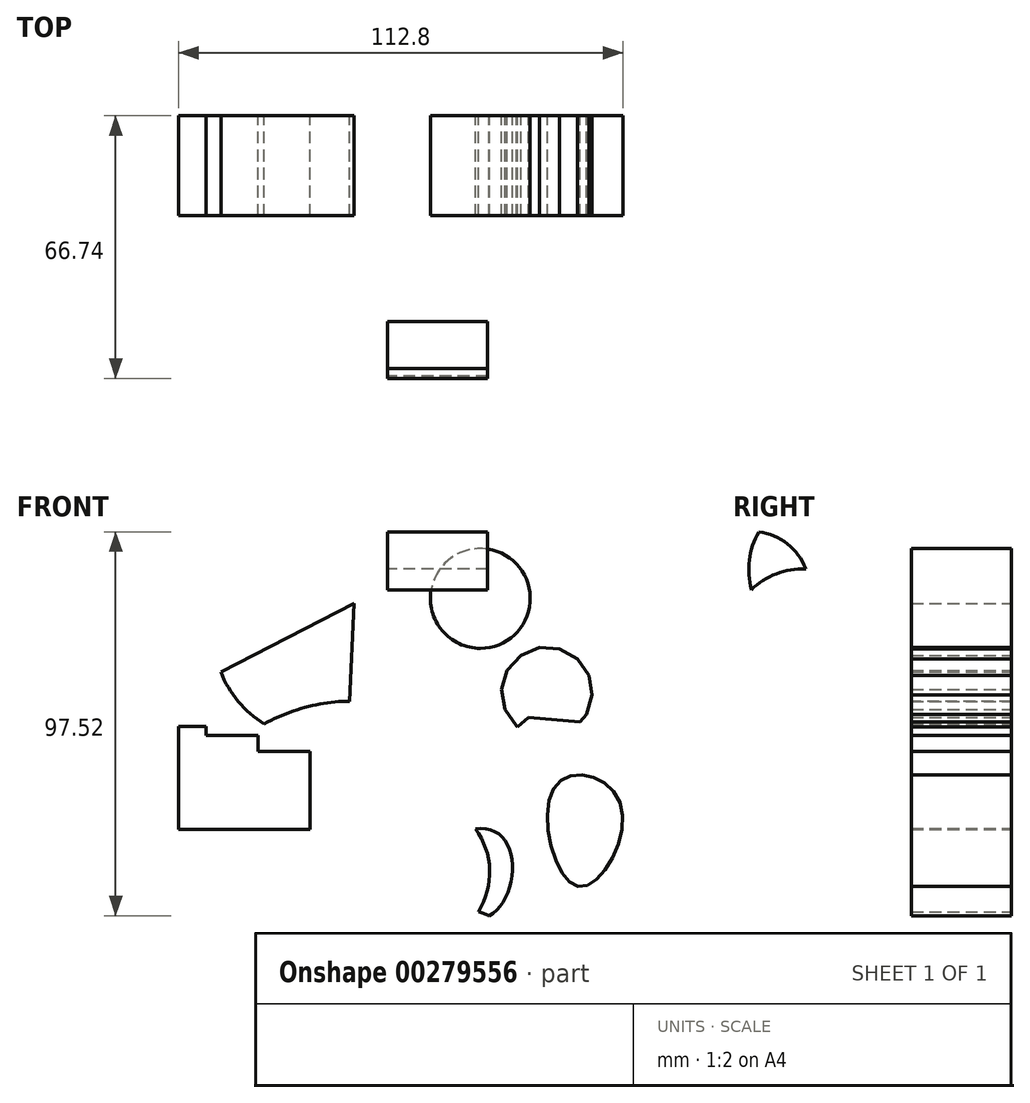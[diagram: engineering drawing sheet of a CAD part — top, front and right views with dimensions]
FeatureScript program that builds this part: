
annotation { "Feature Type Name" : "Feature", "Feature Type Description" : "" }
export const myFeature = defineFeature(function(context is Context, id is Id, definition is map)
    precondition{}
    {
        {
            var Q0;
            Q0=qCreatedBy(makeId("Front.planeOp"),FACE);
            var sketch = newSketch(context, id + "F0", { "sketchPlane" : qUnion([Q0])});
            skLineSegment(sketch, "E0.bottom", {"start": v(-32.94, 21.4) * mm, "end": v(8.82, 21.4) * mm});
            skLineSegment(sketch, "E0.top", {"start": v(-32.94, 0) * mm, "end": v(8.82, 0) * mm});
            skLineSegment(sketch, "E0.left", {"start": v(-32.94, 21.4) * mm, "end": v(-32.94, 0) * mm});
            skLineSegment(sketch, "E0.right", {"start": v(8.82, 21.4) * mm, "end": v(8.82, 0) * mm});
            skLineSegment(sketch, "E1.bottom", {"start": v(-30.86, 26.84) * mm, "end": v(-60.43, 26.84) * mm});
            skLineSegment(sketch, "E1.top", {"start": v(-30.86, 57.19) * mm, "end": v(-60.43, 57.19) * mm});
            skLineSegment(sketch, "E1.left", {"start": v(-30.86, 26.84) * mm, "end": v(-30.86, 57.19) * mm});
            skLineSegment(sketch, "E1.right", {"start": v(-60.43, 26.84) * mm, "end": v(-60.43, 57.19) * mm});
            skLineSegment(sketch, "E2.bottom", {"start": v(-23.6, 31) * mm, "end": v(-46.16, 31) * mm});
            skLineSegment(sketch, "E2.top", {"start": v(-23.6, 4.02) * mm, "end": v(-46.16, 4.02) * mm});
            skLineSegment(sketch, "E2.left", {"start": v(-23.6, 31) * mm, "end": v(-23.6, 4.02) * mm});
            skLineSegment(sketch, "E2.right", {"start": v(-46.16, 31) * mm, "end": v(-46.16, 4.02) * mm});
            skLineSegment(sketch, "E3.bottom", {"start": v(-19.71, 6.35) * mm, "end": v(-53.07, 6.35) * mm});
            skLineSegment(sketch, "E3.top", {"start": v(-19.71, -19.87) * mm, "end": v(-53.07, -19.87) * mm});
            skLineSegment(sketch, "E3.left", {"start": v(-19.71, 6.35) * mm, "end": v(-19.71, -19.87) * mm});
            skLineSegment(sketch, "E3.right", {"start": v(-53.07, 6.35) * mm, "end": v(-53.07, -19.87) * mm});
            skCircle(sketch, "E4", {"center": v(23.53, 38.83) * mm, "radius": 12.68 * mm});
            skArc(sketch, "E5", {"start": v(23.04, -40.76) * mm, "mid": v(1.69, -12.97) * mm, "end": v(0, -47.97) * mm});
            skArc(sketch, "E6", {"start": v(1.69, -47.97) * mm, "mid": v(23.61, -77.66) * mm, "end": v(23.04, -40.76) * mm});
            skPoint(sketch, "E6.startSnap0", {"position": v(1.69, -12.97) * mm});
            skCircle(sketch, "E7.cCircle", {"center": v(40.45, 14.95) * mm, "radius": 11.25 * mm, "construction": true});
            skLineSegment(sketch, "E7.0", {"start": v(48.17, 23.52) * mm, "end": v(51.12, 19.32) * mm});
            skLineSegment(sketch, "E7.1", {"start": v(51.12, 19.32) * mm, "end": v(51.96, 14.25) * mm});
            skLineSegment(sketch, "E7.2", {"start": v(51.96, 14.25) * mm, "end": v(50.52, 9.33) * mm});
            skLineSegment(sketch, "E7.3", {"start": v(50.52, 9.33) * mm, "end": v(47.08, 5.51) * mm});
            skLineSegment(sketch, "E7.4", {"start": v(47.08, 5.51) * mm, "end": v(42.33, 3.57) * mm});
            skLineSegment(sketch, "E7.5", {"start": v(42.33, 3.57) * mm, "end": v(37.2, 3.88) * mm});
            skLineSegment(sketch, "E7.6", {"start": v(37.2, 3.88) * mm, "end": v(32.72, 6.39) * mm});
            skLineSegment(sketch, "E7.7", {"start": v(32.72, 6.39) * mm, "end": v(29.77, 10.59) * mm});
            skLineSegment(sketch, "E7.8", {"start": v(29.77, 10.59) * mm, "end": v(28.93, 15.65) * mm});
            skLineSegment(sketch, "E7.9", {"start": v(28.93, 15.65) * mm, "end": v(30.37, 20.58) * mm});
            skLineSegment(sketch, "E7.10", {"start": v(30.37, 20.58) * mm, "end": v(33.81, 24.4) * mm});
            skLineSegment(sketch, "E7.11", {"start": v(33.81, 24.4) * mm, "end": v(38.57, 26.34) * mm});
            skLineSegment(sketch, "E7.12", {"start": v(38.57, 26.34) * mm, "end": v(43.7, 26.02) * mm});
            skLineSegment(sketch, "E7.13", {"start": v(43.7, 26.02) * mm, "end": v(48.17, 23.52) * mm});
            skPoint(sketch, "E7.0.midPoint", {"position": v(49.65, 21.42) * mm});
            skCircle(sketch, "E8.cCircle", {"center": v(45.67, -22.35) * mm, "radius": 30 * mm, "construction": true});
            skLineSegment(sketch, "E8.0", {"start": v(74.55, -37.2) * mm, "end": v(55.6, -53.27) * mm});
            skLineSegment(sketch, "E8.1", {"start": v(55.6, -53.27) * mm, "end": v(30.82, -51.23) * mm});
            skLineSegment(sketch, "E8.2", {"start": v(30.82, -51.23) * mm, "end": v(14.75, -32.28) * mm});
            skLineSegment(sketch, "E8.3", {"start": v(14.75, -32.28) * mm, "end": v(16.8, -7.5) * mm});
            skLineSegment(sketch, "E8.4", {"start": v(16.8, -7.5) * mm, "end": v(35.75, 8.56) * mm});
            skLineSegment(sketch, "E8.5", {"start": v(35.75, 8.56) * mm, "end": v(60.52, 6.52) * mm});
            skLineSegment(sketch, "E8.6", {"start": v(60.52, 6.52) * mm, "end": v(76.59, -12.43) * mm});
            skLineSegment(sketch, "E8.7", {"start": v(76.59, -12.43) * mm, "end": v(74.55, -37.2) * mm});
            skPoint(sketch, "E8.0.midPoint", {"position": v(65.07, -45.24) * mm});
            skFitSpline(sketch, "E9", {"points": [v(48.4, -34.3) * mm, v(42.68, -8.68) * mm, v(59.1, -13.15) * mm, v(48.4, -34.3) * mm]});
            skFitSpline(sketch, "E10", {"points": [v(28.01, -20.86) * mm, v(7.27, -30.78) * mm, v(25.7, -41.79) * mm, v(28.01, -20.86) * mm]});
            skSolve(sketch);
        }
        {
            var Q0;
            Q0=qCreatedBy(makeId("Front.planeOp"),FACE);
            var sketch = newSketch(context, id + "F1", { "sketchPlane" : qUnion([Q0])});
            skCircle(sketch, "E11.cCircle", {"center": v(-31.68, 57.98) * mm, "radius": 11.74 * mm, "construction": true});
            skLineSegment(sketch, "E11.0", {"start": v(-24.72, 48.53) * mm, "end": v(-43.35, 56.68) * mm});
            skLineSegment(sketch, "E11.1", {"start": v(-43.35, 56.68) * mm, "end": v(-26.98, 68.74) * mm});
            skLineSegment(sketch, "E11.2", {"start": v(-26.98, 68.74) * mm, "end": v(-24.72, 48.53) * mm});
            skCircle(sketch, "E12.cCircle", {"center": v(-37.65, -7.68) * mm, "radius": 53.81 * mm, "construction": true});
            skLineSegment(sketch, "E12.0", {"start": v(-8.55, 37.59) * mm, "end": v(-13, -55.51) * mm});
            skLineSegment(sketch, "E12.1", {"start": v(-13, -55.51) * mm, "end": v(-91.4, -5.11) * mm});
            skLineSegment(sketch, "E12.2", {"start": v(-91.4, -5.11) * mm, "end": v(-8.55, 37.59) * mm});
            skArc(sketch, "E13", {"start": v(32.74, -7.43) * mm, "mid": v(41.22, -6.44) * mm, "end": v(48.7, -2.28) * mm});
            skArc(sketch, "E14", {"start": v(32.74, -7.43) * mm, "mid": v(27.73, 35.35) * mm, "end": v(48.7, -2.28) * mm});
            skArc(sketch, "E15", {"start": v(-64.01, 33.1) * mm, "mid": v(-67.99, 39.01) * mm, "end": v(-68.26, 46.12) * mm});
            skEllipse(sketch, "E16", {"center": v(-20.24, -7.43) * mm, "majorRadius": 29.75 * mm, "minorRadius": 17.83 * mm, "majorAxis": v(0.92, 0.4)});
            skEllipse(sketch, "E17", {"center": v(-72.47, 19.68) * mm, "majorRadius": 20.15 * mm, "minorRadius": 2.66 * mm, "majorAxis": v(0.81, -0.58)});
            skCircle(sketch, "E18", {"center": v(-19.65, 16.58) * mm, "radius": 40.5 * mm});
            skPoint(sketch, "E18.first.point", {"position": v(-6.06, 54.75) * mm});
            skPoint(sketch, "E18.second.point", {"position": v(20.05, 24.65) * mm});
            skPoint(sketch, "E18.third.point", {"position": v(15.94, -2.78) * mm});
            skCircle(sketch, "E19", {"center": v(-17.14, 30) * mm, "radius": 27.1 * mm});
            skPoint(sketch, "E19.second.point", {"position": v(-44.12, 32.61) * mm});
            skPoint(sketch, "E19.third.point", {"position": v(-42.38, 20.15) * mm});
            skLineSegment(sketch, "E20.bottom", {"start": v(-12.3, -41.02) * mm, "end": v(-75.35, -41.02) * mm});
            skLineSegment(sketch, "E20.top", {"start": v(-12.3, -30.37) * mm, "end": v(-75.35, -30.37) * mm});
            skLineSegment(sketch, "E20.left", {"start": v(-12.3, -41.02) * mm, "end": v(-12.3, -30.37) * mm});
            skLineSegment(sketch, "E20.right", {"start": v(-75.35, -41.02) * mm, "end": v(-75.35, -30.37) * mm});
            skPoint(sketch, "E20.middle", {"position": v(-43.83, -35.7) * mm});
            skLineSegment(sketch, "E21.bottom", {"start": v(-43.83, -47.72) * mm, "end": v(-43.83, -47.72) * mm});
            skLineSegment(sketch, "E21.top", {"start": v(-43.83, -23.67) * mm, "end": v(-43.83, -23.67) * mm});
            skLineSegment(sketch, "E21.left", {"start": v(-43.83, -47.72) * mm, "end": v(-43.83, -23.67) * mm});
            skLineSegment(sketch, "E21.right", {"start": v(-43.83, -47.72) * mm, "end": v(-43.83, -23.67) * mm});
            skPoint(sketch, "E21.cornerSnap0", {"position": v(-43.83, -41.02) * mm});
            skLineSegment(sketch, "E22.bottom", {"start": v(-62.27, -35.7) * mm, "end": v(-25.38, -35.7) * mm});
            skLineSegment(sketch, "E22.top", {"start": v(-62.27, -11.64) * mm, "end": v(-25.38, -11.64) * mm});
            skLineSegment(sketch, "E22.left", {"start": v(-62.27, -35.7) * mm, "end": v(-62.27, -11.64) * mm});
            skLineSegment(sketch, "E22.right", {"start": v(-25.38, -35.7) * mm, "end": v(-25.38, -11.64) * mm});
            skPoint(sketch, "E22.middle", {"position": v(-43.83, -23.67) * mm});
            skLineSegment(sketch, "E23.bottom", {"start": v(25.03, -9.67) * mm, "end": v(-2.83, -9.67) * mm});
            skLineSegment(sketch, "E23.top", {"start": v(25.03, -109.65) * mm, "end": v(-2.83, -109.65) * mm});
            skLineSegment(sketch, "E23.left", {"start": v(25.03, -9.67) * mm, "end": v(25.03, -109.65) * mm});
            skLineSegment(sketch, "E23.right", {"start": v(-2.83, -9.67) * mm, "end": v(-2.83, -109.65) * mm});
            skPoint(sketch, "E23.middle", {"position": v(11.1, -59.66) * mm});
            skSolve(sketch);
        }
        {
            var Q0;
            Q0=makeQuery(id+"F0.imprint","IMPRINT",FACE,{"disambiguationData":[TD([[makeQuery(id+"F0.imprint","IMPRINT",EDGE,{"derivedFrom":sQuery(id+"F0.wireOp",EDGE,"E4")}),1.0]])]});
            var Q1;
            Q1=makeQuery(id+"F0.imprint","IMPRINT",FACE,{"disambiguationData":[TD([[makeQuery(id+"F0.imprint","IMPRINT",EDGE,{"derivedFrom":sQuery(id+"F0.wireOp",EDGE,"E7.0")}),-1.0]])]});
            var Q2;
            {var subQ0=sQuery(id+"F0.wireOp",EDGE,"E6");var subQ1=sQuery(id+"F0.wireOp",EDGE,"E5");var subQ2=makeQuery(id+"F0.imprint","INTERSECT",VERTEX,{"derivedFrom":[subQ1,subQ0]});Q2=makeQuery(id+"F0.imprint","IMPRINT",FACE,{"disambiguationData":[TD([[makeQuery(id+"F0.imprint","IMPRINT",EDGE,{"disambiguationData":[TD([[subQ2,-1.0]])],"derivedFrom":subQ1}),-1.0]])]});}
            var Q3;
            {var subQ12=sQuery(id+"F0.wireOp",EDGE,"E3.top");Q3=makeQuery(id+"F0.imprint","IMPRINT",FACE,{"disambiguationData":[TD([[makeQuery(id+"F0.imprint","IMPRINT",EDGE,{"derivedFrom":subQ12}),-1.0]])]});}
            var Q4;
            {var subQ0=sQuery(id+"F1.wireOp",EDGE,"E12.2");var subQ1=sQuery(id+"F1.wireOp",EDGE,"E12.0");var subQ2=makeQuery(id+"F1.imprint","INTERSECT",VERTEX,{"derivedFrom":[subQ1,subQ0]});Q4=makeQuery(id+"F1.imprint","IMPRINT",FACE,{"disambiguationData":[TD([[makeQuery(id+"F1.imprint","IMPRINT",EDGE,{"disambiguationData":[TD([[subQ2,-1.0]])],"derivedFrom":subQ1}),-1.0]])]});}
            var Q5;
            Q5=makeQuery(id+"F0.imprint","IMPRINT",FACE,{"disambiguationData":[TD([[makeQuery(id+"F0.imprint","IMPRINT",EDGE,{"derivedFrom":sQuery(id+"F0.wireOp",EDGE,"E9")}),-1.0]])]});
            extrude(context, id + "F2", {"entities" : qUnion([Q0, Q1, Q2, Q3, Q4, Q5]), "depth" : 25.4 * mm});
        }
        {
            var Q0;
            Q0=qCreatedBy(makeId("Right.planeOp"),FACE);
            var sketch = newSketch(context, id + "F3", { "sketchPlane" : qUnion([Q0])});
            skArc(sketch, "E24", {"start": v(-52.91, 27.42) * mm, "mid": v(-33.21, 59.63) * mm, "end": v(-66.08, 41.05) * mm});
            skArc(sketch, "E25", {"start": v(-66.08, 41.05) * mm, "mid": v(-35.47, 20.02) * mm, "end": v(-71.86, 27.42) * mm});
            skArc(sketch, "E26", {"start": v(-71.86, 27.42) * mm, "mid": v(-58.73, 53.9) * mm, "end": v(-74.9, 29.15) * mm});
            skArc(sketch, "E27", {"start": v(-74.9, 29.15) * mm, "mid": v(-90.16, -1.05) * mm, "end": v(-71.86, 27.42) * mm});
            skSolve(sketch);
        }
        {
            var Q0;
            {var subQ0=sQuery(id+"F3.wireOp",EDGE,"E25");var subQ1=sQuery(id+"F3.wireOp",EDGE,"E24");var subQ2=makeQuery(id+"F3.imprint","INTERSECT",VERTEX,{"disambiguationData":[OD(1.0)],"derivedFrom":[subQ1,subQ0]});Q0=makeQuery(id+"F3.imprint","IMPRINT",FACE,{"disambiguationData":[TD([[makeQuery(id+"F3.imprint","IMPRINT",EDGE,{"disambiguationData":[TD([[subQ2,-1.0]])],"derivedFrom":subQ1}),1.0]])]});}
            var Q1;
            {var subQ0=sQuery(id+"F3.wireOp",EDGE,"E25");var subQ1=sQuery(id+"F3.wireOp",EDGE,"E24");var subQ2=makeQuery(id+"F3.imprint","INTERSECT",VERTEX,{"disambiguationData":[OD(0.0)],"derivedFrom":[subQ1,subQ0]});Q1=makeQuery(id+"F3.imprint","IMPRINT",FACE,{"disambiguationData":[TD([[makeQuery(id+"F3.imprint","IMPRINT",EDGE,{"disambiguationData":[TD([[subQ2,1.0]])],"derivedFrom":subQ1}),1.0]])]});}
            var Q2;
            {var subQ0=sQuery(id+"F3.wireOp",EDGE,"E27");var subQ1=sQuery(id+"F3.wireOp",EDGE,"E25");var subQ3=makeQuery(id+"F3.imprint","INTERSECT",VERTEX,{"derivedFrom":[subQ1,subQ0]});Q2=makeQuery(id+"F3.imprint","IMPRINT",FACE,{"disambiguationData":[TD([[makeQuery(id+"F3.imprint","IMPRINT",EDGE,{"disambiguationData":[TD([[subQ3,-1.0]])],"derivedFrom":subQ1}),-1.0]])]});}
            var Q3;
            {var subQ0=sQuery(id+"F3.wireOp",EDGE,"E25");var subQ1=makeQuery(id+"F3.imprint","INTERSECT",VERTEX,{"disambiguationData":[OD(1.0)],"derivedFrom":[sQuery(id+"F3.wireOp",EDGE,"E24"),subQ0]});Q3=makeQuery(id+"F3.imprint","IMPRINT",FACE,{"disambiguationData":[TD([[makeQuery(id+"F3.imprint","IMPRINT",EDGE,{"disambiguationData":[TD([[subQ1,1.0]])],"derivedFrom":subQ0}),-1.0]])]});}
            var Q4;
            {var subQ2=sQuery(id+"F3.wireOp",EDGE,"E25");var subQ5=sQuery(id+"F3.wireOp",EDGE,"E24");var subQ6=makeQuery(id+"F3.imprint","INTERSECT",VERTEX,{"disambiguationData":[OD(0.0)],"derivedFrom":[subQ5,subQ2]});Q4=makeQuery(id+"F3.imprint","IMPRINT",FACE,{"disambiguationData":[TD([[makeQuery(id+"F3.imprint","IMPRINT",EDGE,{"disambiguationData":[TD([[subQ6,1.0]])],"derivedFrom":subQ5}),-1.0]])]});}
            extrude(context, id + "F4", {"entities" : qUnion([Q0, Q1, Q2, Q3, Q4]), "depth" : 25.4 * mm});
        }
    });
